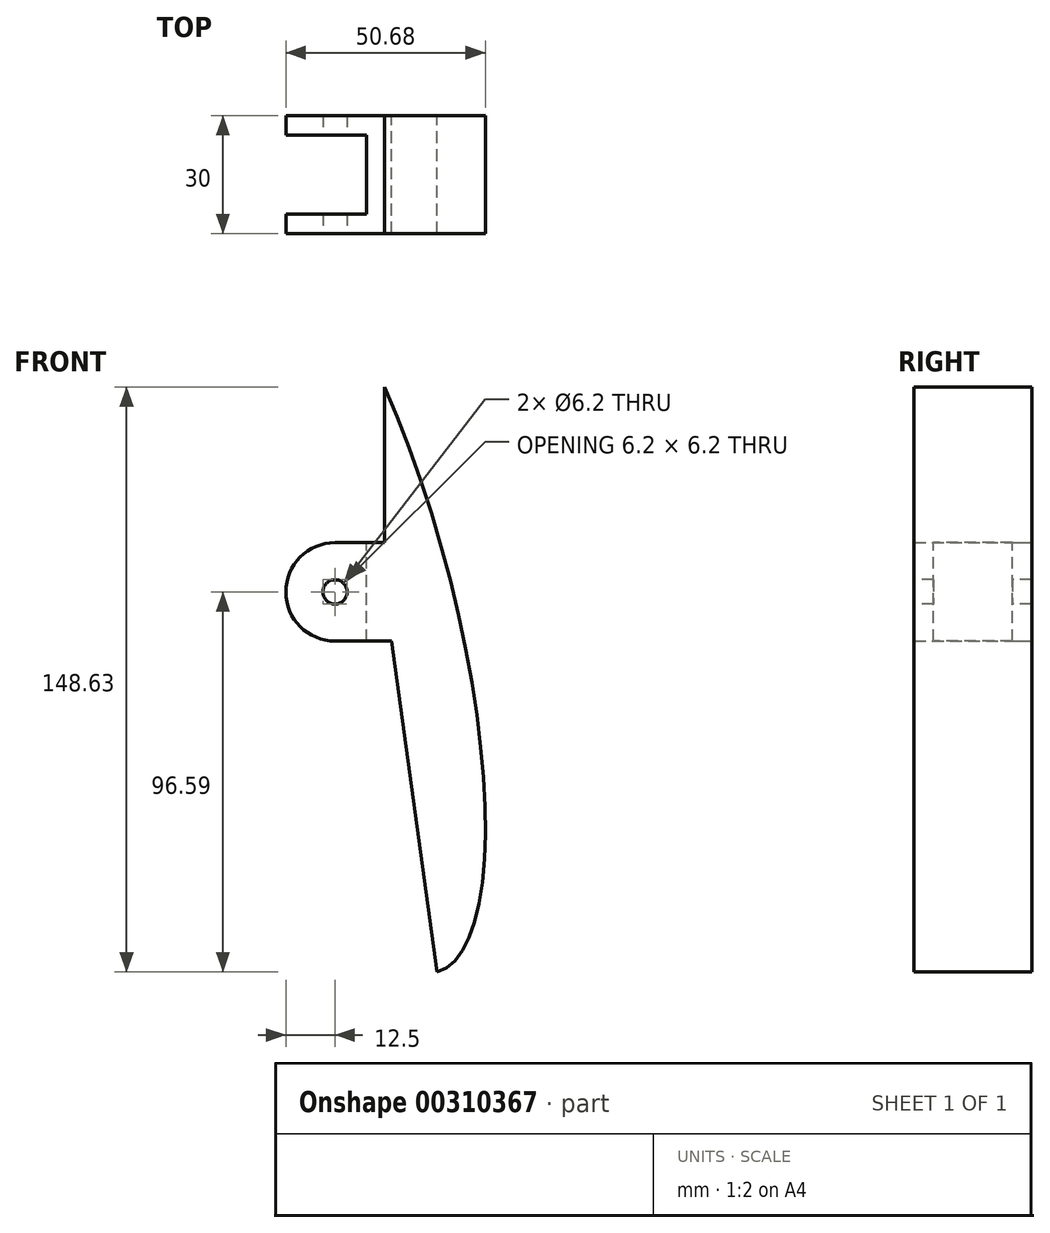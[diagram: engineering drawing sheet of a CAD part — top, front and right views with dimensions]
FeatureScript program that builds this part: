
annotation { "Feature Type Name" : "Feature", "Feature Type Description" : "" }
export const myFeature = defineFeature(function(context is Context, id is Id, definition is map)
    precondition{}
    {
        {
            var Q0;
            Q0=qCreatedBy(makeId("Front.planeOp"),FACE);
            var sketch = newSketch(context, id + "F0", { "sketchPlane" : qUnion([Q0])});
            skCircle(sketch, "E0", {"center": v(0, 0) * mm, "radius": 12.5 * mm});
            skLineSegment(sketch, "E1", {"start": v(0, 0) * mm, "end": v(25.98, 15) * mm, "construction": true});
            skLineSegment(sketch, "E2", {"start": v(0, 0) * mm, "end": v(30, 0) * mm, "construction": true});
            skEllipticalArc(sketch, "E3", {});
            skLineSegment(sketch, "E4", {"start": v(25.88, -96.6) * mm, "end": v(12.62, 0) * mm});
            skLineSegment(sketch, "E5", {"start": v(12.62, 0) * mm, "end": v(12.62, 52.04) * mm});
            skLineSegment(sketch, "E6", {"start": v(0, -12.5) * mm, "end": v(14.33, -12.5) * mm});
            skLineSegment(sketch, "E7", {"start": v(0, 12.5) * mm, "end": v(12.62, 12.5) * mm});
            const initialGuessF0  = {"E3": [0, 0, -0.2588190451025213, 0.9659258262890682, 0.1, 0.029065523183215678, 3.141592653589793, 5.201656849775983]};
            skSetInitialGuess(sketch, initialGuessF0);
            skSolve(sketch);
        }
        {
            var Q0;
            Q0 = qSketchRegion(id + "F0", true);
            extrude(context, id + "F1", {"entities" : qUnion([Q0]), "endBound" : BoundingType.SYMMETRIC, "depth" : 30 * mm});
        }
        {
            var Q0;
            Q0=makeQuery(id+"F1.opExtrude","SWEPT_FACE",FACE,{"disambiguationData":[OSD([sQuery(id+"F0.wireOp",EDGE,"E7")])]});
            var sketch = newSketch(context, id + "F2", { "sketchPlane" : qUnion([Q0])});
            skLineSegment(sketch, "E8.bottom", {"start": v(0, 10) * mm, "end": v(-19.23, 10) * mm});
            skLineSegment(sketch, "E8.top", {"start": v(0, -10) * mm, "end": v(-19.23, -10) * mm});
            skLineSegment(sketch, "E8.left", {"start": v(0, 10) * mm, "end": v(0, -10) * mm});
            skLineSegment(sketch, "E8.right", {"start": v(-19.23, 10) * mm, "end": v(-19.23, -10) * mm});
            skLineSegment(sketch, "E9", {"start": v(0, 10) * mm, "end": v(8, 10) * mm});
            skLineSegment(sketch, "E10", {"start": v(8, 10) * mm, "end": v(8, -10) * mm});
            skLineSegment(sketch, "E11", {"start": v(8, -10) * mm, "end": v(0, -10) * mm});
            skSolve(sketch);
        }
        {
            var Q0;
            Q0 = qSketchRegion(id + "F2", true);
            extrude(context, id + "F3", {"entities" : qUnion([Q0]), "operationType" : NewBodyOperationType.REMOVE, "endBound" : BoundingType.THROUGH_ALL, "oppositeDirection" : true, "depth" : 25 * mm});
        }
        {
            var Q0;
            Q0=makeQuery(id+"F1.opExtrude","CAP_FACE",FACE,{"disambiguationData":[OSD([sQuery(id+"F0.wireOp",EDGE,"E0"),sQuery(id+"F0.wireOp",EDGE,"E3"),sQuery(id+"F0.wireOp",EDGE,"E4"),sQuery(id+"F0.wireOp",EDGE,"E5"),sQuery(id+"F0.wireOp",EDGE,"E6"),sQuery(id+"F0.wireOp",EDGE,"E7")])],"isStart":false});
            var sketch = newSketch(context, id + "F4", { "sketchPlane" : qUnion([Q0])});
            skCircle(sketch, "E12", {"center": v(0, 0) * mm, "radius": 3.1 * mm});
            skSolve(sketch);
        }
        {
            var Q0;
            Q0 = qSketchRegion(id + "F4", true);
            extrude(context, id + "F5", {"entities" : qUnion([Q0]), "operationType" : NewBodyOperationType.ADD, "depth" : 25 * mm});
        }
        {
            var Q0;
            Q0=makeQuery(id+"F5.opExtrude","CAP_FACE",FACE,{"disambiguationData":[OSD([sQuery(id+"F4.wireOp",EDGE,"E12")])],"isStart":false});
            extrude(context, id + "F6", {"entities" : qUnion([Q0]), "operationType" : NewBodyOperationType.REMOVE, "endBound" : BoundingType.THROUGH_ALL, "oppositeDirection" : true, "depth" : 25 * mm});
        }
    });
